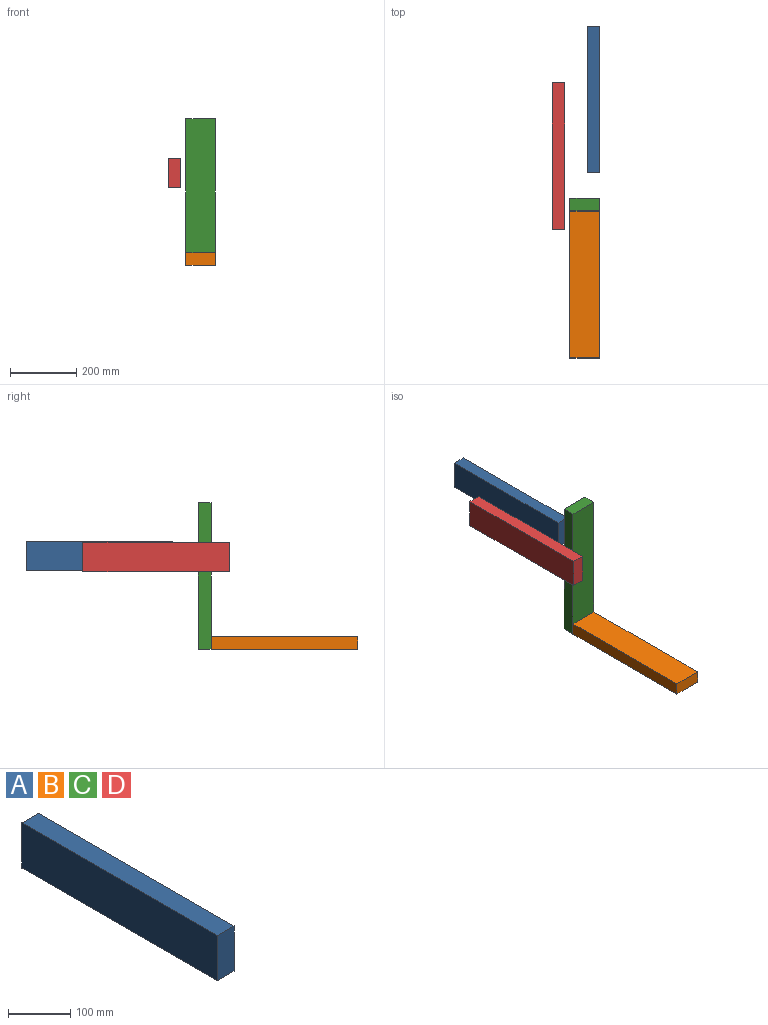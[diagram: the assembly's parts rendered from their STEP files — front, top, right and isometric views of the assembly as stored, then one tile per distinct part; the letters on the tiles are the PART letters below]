
ASSEMBLY  parts=4 mates=1
PART A: 6 faces, bbox 38.1x444.5x88.9 mm
  f0: plane 444.5x88.9mm, normal (-1,0,0), area 39516.1mm2, adj f1,f3,f4,f5
  f1: plane 444.5x38.1mm, normal (0,0,-1), area 16935.5mm2, adj f0,f2,f4,f5
  f2: plane 444.5x88.9mm, normal (1,0,0), area 39516.1mm2, adj f1,f3,f4,f5
  f3: plane 444.5x38.1mm, normal (0,0,1), area 16935.5mm2, adj f0,f2,f4,f5
  f4: plane 88.9x38.1mm, normal (0,-1,0), area 3387.1mm2, adj f0,f1,f2,f3
  f5: plane 88.9x38.1mm, normal (0,1,0), area 3387.1mm2, adj f0,f1,f2,f3
PART B: same geometry as A
PART C: same geometry as A
PART D: same geometry as A
PLACE A t=(-31.86,295.47,-85.51)mm
PLACE B rot(axis=(0.71,0,0.71),180deg) t=(-84.21,-708.7,-324.74)mm
PLACE C rot(axis=(-0.58,0.58,-0.58),120deg) t=(-84.21,-226.1,-324.74)mm
PLACE D t=(-137.85,123.71,-89.38)mm
MATE planar B.f4 <-> C.f2  axis (0,1,0) through (-39.76,-264.2,-305.69)mm
